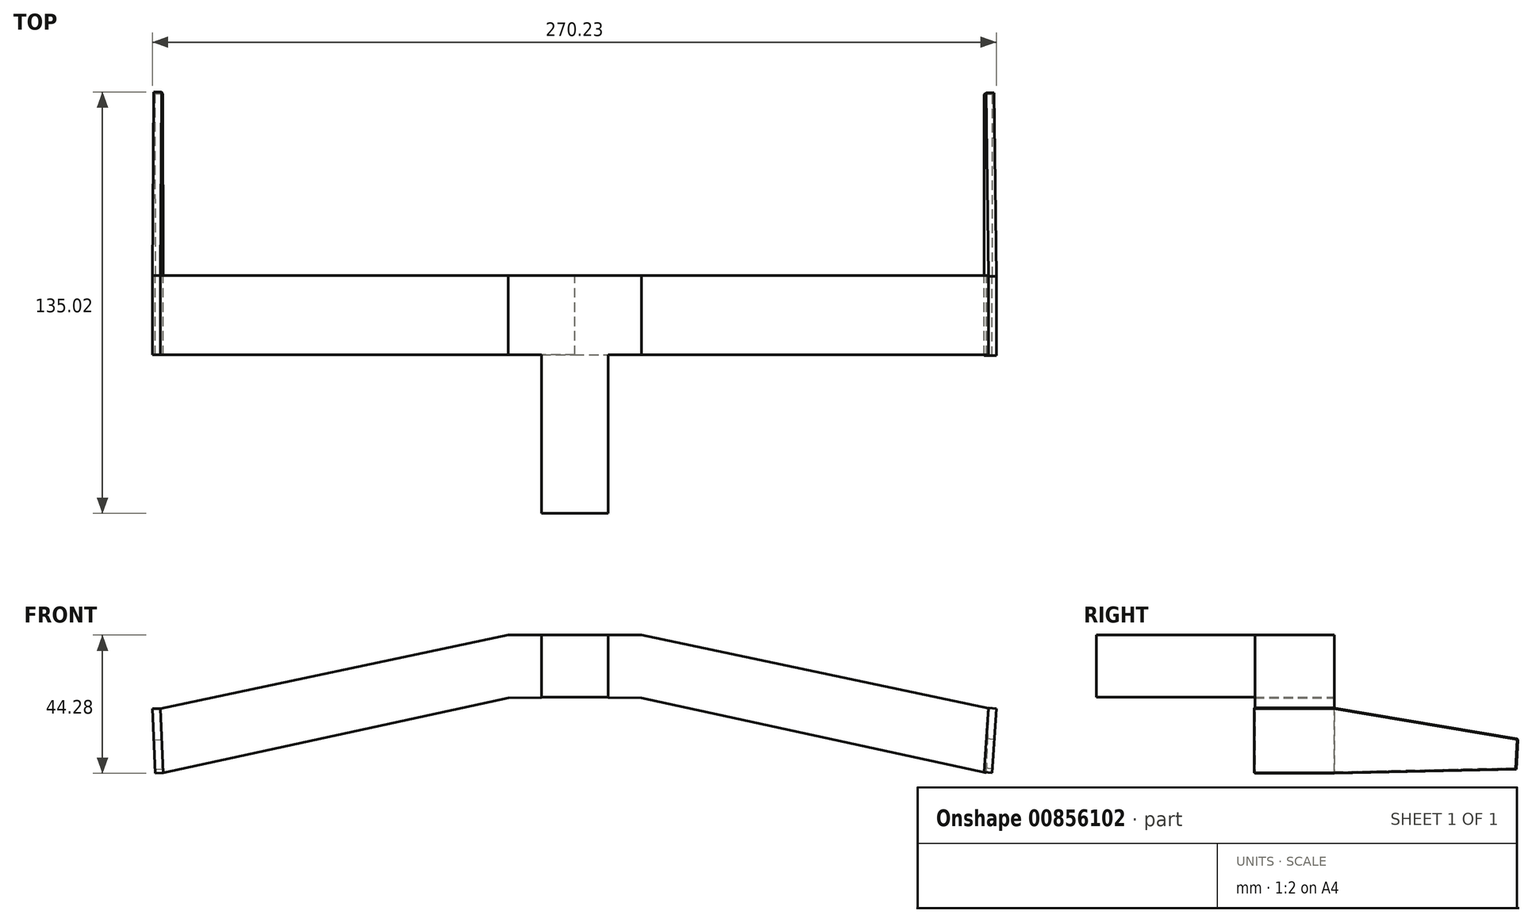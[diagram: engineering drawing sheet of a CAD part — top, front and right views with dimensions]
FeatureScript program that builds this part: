
annotation { "Feature Type Name" : "Feature", "Feature Type Description" : "" }
export const myFeature = defineFeature(function(context is Context, id is Id, definition is map)
    precondition{}
    {
        {
            var Q0;
            Q0=qCreatedBy(makeId("Front.planeOp"),FACE);
            var sketch = newSketch(context, id + "F0", { "sketchPlane" : qUnion([Q0])});
            skLineSegment(sketch, "E0", {"start": v(21.32, 0) * mm, "end": v(0, 0) * mm});
            skLineSegment(sketch, "E1", {"start": v(0, 0) * mm, "end": v(0, -19.96) * mm});
            skLineSegment(sketch, "E2", {"start": v(0, -19.96) * mm, "end": v(21.32, -20.13) * mm});
            skLineSegment(sketch, "E3", {"start": v(21.32, -20.13) * mm, "end": v(131.84, -44.18) * mm});
            skLineSegment(sketch, "E4", {"start": v(131.84, -44.18) * mm, "end": v(132.7, -23.54) * mm});
            skLineSegment(sketch, "E5", {"start": v(132.7, -23.54) * mm, "end": v(21.32, 0) * mm});
            skSolve(sketch);
        }
        {
            var Q0;
            Q0=makeQuery(id+"F0.imprint","IMPRINT",FACE,{"disambiguationData":[TD([[makeQuery(id+"F0.imprint","IMPRINT",EDGE,{"derivedFrom":sQuery(id+"F0.wireOp",EDGE,"E0")}),1.0]])]});
            var sketch = newSketch(context, id + "F1", { "sketchPlane" : qUnion([Q0])});
            skSolve(sketch);
        }
        {
            var Q0;
            Q0=makeQuery(id+"F1.imprint","IMPRINT",FACE,{"disambiguationData":[TD([[makeQuery(id+"F1.imprint","IMPRINT",EDGE,{"derivedFrom":makeQuery(id+"F0.imprint","IMPRINT",EDGE,{"derivedFrom":sQuery(id+"F0.wireOp",EDGE,"E0")})}),1.0]])]});
            extrude(context, id + "F2", {"entities" : qUnion([Q0]), "depth" : 25.4 * mm, "offsetDistance" : 25.4 * mm});
        }
        {
            var Q0;
            Q0=makeQuery(id+"F2.opExtrude","SWEPT_BODY",BODY,{"disambiguationData":[OSD([sQuery(id+"F0.wireOp",EDGE,"E0"),sQuery(id+"F0.wireOp",EDGE,"E1"),sQuery(id+"F0.wireOp",EDGE,"E2"),sQuery(id+"F0.wireOp",EDGE,"E3"),sQuery(id+"F0.wireOp",EDGE,"E4"),sQuery(id+"F0.wireOp",EDGE,"E5")])]});
            var Q1;
            Q1=makeQuery(id+"F2.opExtrude","SWEPT_FACE",FACE,{"disambiguationData":[OSD([sQuery(id+"F0.wireOp",EDGE,"E1")])]});
            mirror(context, id + "F3", {"operationType" : NewBodyOperationType.ADD, "entities" : qUnion([Q0]), "mirrorPlane" : qUnion([Q1])});
        }
        {
            var Q0;
            {var subQ0=makeQuery(id+"F2.opExtrude","CAP_FACE",FACE,{"disambiguationData":[OSD([sQuery(id+"F0.wireOp",EDGE,"E0"),sQuery(id+"F0.wireOp",EDGE,"E1"),sQuery(id+"F0.wireOp",EDGE,"E2"),sQuery(id+"F0.wireOp",EDGE,"E3"),sQuery(id+"F0.wireOp",EDGE,"E4"),sQuery(id+"F0.wireOp",EDGE,"E5")])],"isStart":false});Q0=makeQuery(id+"F3.boolean.opBoolean","MERGE",FACE,{"derivedFrom":[subQ0,makeQuery(id+"F3.opPattern","COPY",FACE,{"derivedFrom":subQ0,"instanceName":"1"})]});}
            var sketch = newSketch(context, id + "F4", { "sketchPlane" : qUnion([Q0])});
            skPoint(sketch, "E6.oppositeSnap0", {"position": v(10.66, -20.04) * mm});
            skLineSegment(sketch, "E6.bottom", {"start": v(0, -19.96) * mm, "end": v(10.66, -19.96) * mm});
            skLineSegment(sketch, "E6.top", {"start": v(0, 0) * mm, "end": v(10.66, 0) * mm});
            skLineSegment(sketch, "E6.left", {"start": v(0, -19.96) * mm, "end": v(0, 0) * mm});
            skLineSegment(sketch, "E6.right", {"start": v(10.66, -19.96) * mm, "end": v(10.66, 0) * mm});
            skPoint(sketch, "E7.oppositeSnap0", {"position": v(-10.66, -20.04) * mm});
            skLineSegment(sketch, "E7.bottom", {"start": v(0, -19.96) * mm, "end": v(-10.66, -19.96) * mm});
            skLineSegment(sketch, "E7.top", {"start": v(0, 0) * mm, "end": v(-10.66, 0) * mm});
            skLineSegment(sketch, "E7.right", {"start": v(-10.66, -19.96) * mm, "end": v(-10.66, 0) * mm});
            skSolve(sketch);
        }
        {
            var Q0;
            Q0=makeQuery(id+"F4.imprint","IMPRINT",FACE,{"disambiguationData":[TD([[makeQuery(id+"F4.imprint","IMPRINT",EDGE,{"derivedFrom":sQuery(id+"F4.wireOp",EDGE,"E6.bottom")}),1.0]])]});
            var Q1;
            Q1=makeQuery(id+"F4.imprint","IMPRINT",FACE,{"disambiguationData":[TD([[makeQuery(id+"F4.imprint","IMPRINT",EDGE,{"derivedFrom":sQuery(id+"F4.wireOp",EDGE,"E7.bottom")}),-1.0]])]});
            extrude(context, id + "F5", {"entities" : qUnion([Q0, Q1]), "operationType" : NewBodyOperationType.ADD, "depth" : 50.8 * mm, "offsetDistance" : 25.4 * mm});
        }
        {
            var Q0;
            Q0=makeQuery(id+"F3.opPattern","COPY",FACE,{"derivedFrom":makeQuery(id+"F2.opExtrude","SWEPT_FACE",FACE,{"disambiguationData":[OSD([sQuery(id+"F0.wireOp",EDGE,"E4")])]}),"instanceName":"1"});
            var sketch = newSketch(context, id + "F6", { "sketchPlane" : qUnion([Q0])});
            skLineSegment(sketch, "E8", {"start": v(25.4, -18.04) * mm, "end": v(0, -18.04) * mm});
            skLineSegment(sketch, "E9", {"start": v(0, -18.04) * mm, "end": v(-58.82, -27.97) * mm});
            skLineSegment(sketch, "E10", {"start": v(-58.82, -27.97) * mm, "end": v(-58.32, -37.4) * mm});
            skLineSegment(sketch, "E11", {"start": v(-58.32, -37.4) * mm, "end": v(0, -38.7) * mm});
            skLineSegment(sketch, "E12", {"start": v(0, -38.7) * mm, "end": v(25.4, -38.7) * mm});
            skLineSegment(sketch, "E13", {"start": v(25.4, -38.7) * mm, "end": v(25.4, -18.04) * mm});
            skSolve(sketch);
        }
        {
            var Q0;
            Q0=makeQuery(id+"F6.imprint","IMPRINT",FACE,{"disambiguationData":[TD([[makeQuery(id+"F6.imprint","IMPRINT",EDGE,{"derivedFrom":sQuery(id+"F6.wireOp",EDGE,"E9")}),1.0]])]});
            var Q1;
            Q1=makeQuery(id+"F6.imprint","IMPRINT",FACE,{"disambiguationData":[TD([[makeQuery(id+"F6.imprint","IMPRINT",EDGE,{"derivedFrom":sQuery(id+"F6.wireOp",EDGE,"E8")}),1.0]])]});
            extrude(context, id + "F7", {"entities" : qUnion([Q0, Q1]), "depth" : 2.54 * mm, "offsetDistance" : 25.4 * mm});
        }
        {
            var Q0;
            Q0=makeQuery(id+"F7.opExtrude","SWEPT_BODY",BODY,{"disambiguationData":[OSD([sQuery(id+"F6.wireOp",EDGE,"E8"),sQuery(id+"F6.wireOp",EDGE,"E9"),sQuery(id+"F6.wireOp",EDGE,"E10"),sQuery(id+"F6.wireOp",EDGE,"E11"),sQuery(id+"F6.wireOp",EDGE,"E12"),sQuery(id+"F6.wireOp",EDGE,"E13")])]});
            var Q1;
            Q1=makeQuery(id+"F2.opExtrude","SWEPT_FACE",FACE,{"disambiguationData":[OSD([sQuery(id+"F0.wireOp",EDGE,"E4")])]});
            mirror(context, id + "F8", {"entities" : qUnion([Q0]), "mirrorPlane" : qUnion([Q1])});
        }
        {
            var Q0;
            Q0=makeQuery(id+"F8.opPattern","COPY",BODY,{"derivedFrom":makeQuery(id+"F7.opExtrude","SWEPT_BODY",BODY,{"disambiguationData":[OSD([sQuery(id+"F6.wireOp",EDGE,"E8"),sQuery(id+"F6.wireOp",EDGE,"E9"),sQuery(id+"F6.wireOp",EDGE,"E10"),sQuery(id+"F6.wireOp",EDGE,"E11"),sQuery(id+"F6.wireOp",EDGE,"E12"),sQuery(id+"F6.wireOp",EDGE,"E13")])]}),"instanceName":"1"});
            transform(context, id + "F9", {"entities" : qUnion([Q0]), "transformType" : TransformType.TRANSLATION_3D, "dx" : -263.58 * mm, "dy" : -0.27 * mm, "dz" : 22.1 * mm, "makeCopy" : false});
        }
        {
            var Q0;
            Q0=makeQuery(id+"F8.opPattern","COPY",BODY,{"derivedFrom":makeQuery(id+"F7.opExtrude","SWEPT_BODY",BODY,{"disambiguationData":[OSD([sQuery(id+"F6.wireOp",EDGE,"E8"),sQuery(id+"F6.wireOp",EDGE,"E9"),sQuery(id+"F6.wireOp",EDGE,"E10"),sQuery(id+"F6.wireOp",EDGE,"E11"),sQuery(id+"F6.wireOp",EDGE,"E12"),sQuery(id+"F6.wireOp",EDGE,"E13")])]}),"instanceName":"1"});
            var Q1;
            Q1=makeQuery(id+"F8.opPattern","COPY",EDGE,{"derivedFrom":makeQuery(id+"F7.opExtrude","CAP_EDGE",EDGE,{"disambiguationData":[OSD([sQuery(id+"F6.wireOp",EDGE,"E12")])],"isStart":false}),"instanceName":"1"});
            transform(context, id + "F10", {"entities" : qUnion([Q0]), "transformType" : TransformType.ROTATION, "transformAxis" : qUnion([Q1]), "angle" : 3.14 * degree, "oppositeDirection" : true, "makeCopy" : false});
        }
    });
